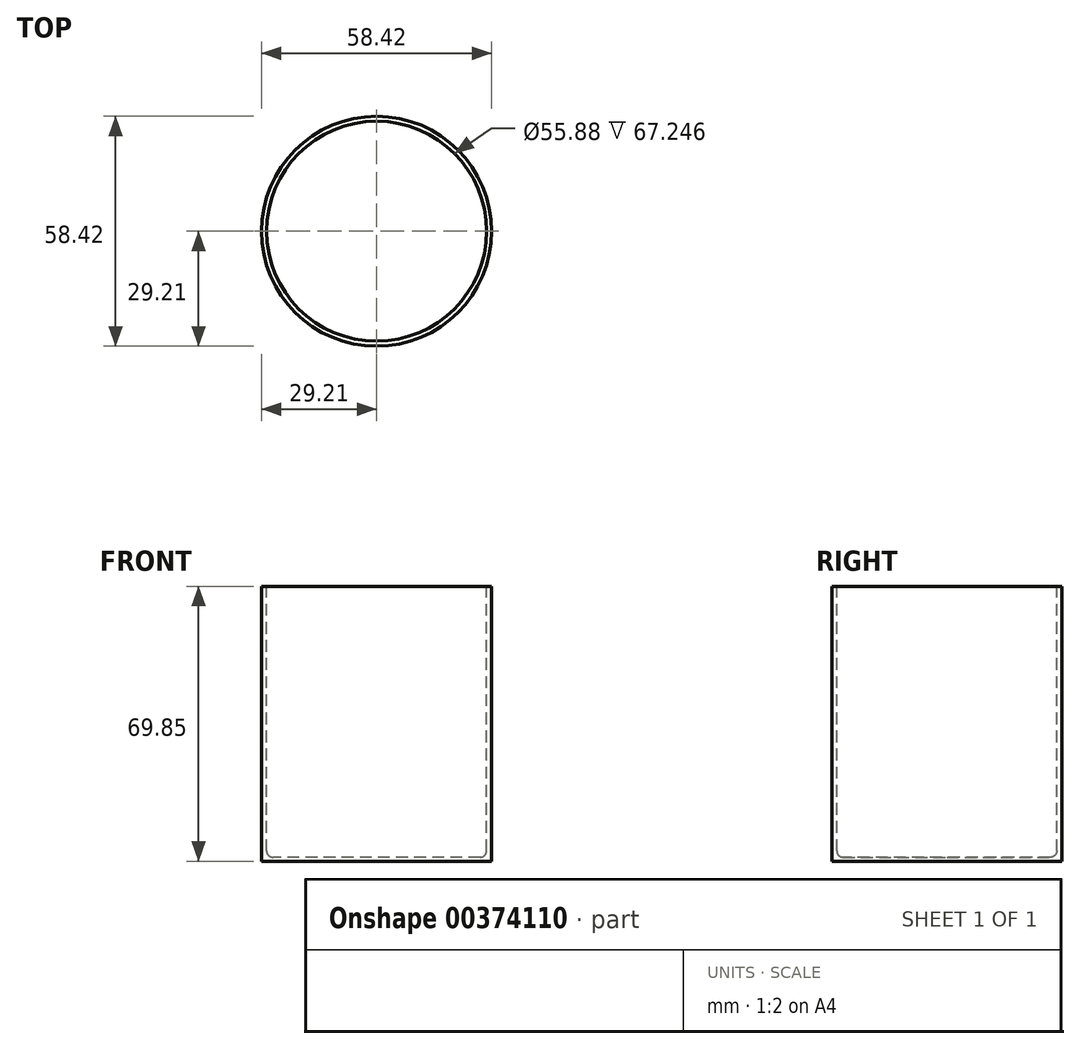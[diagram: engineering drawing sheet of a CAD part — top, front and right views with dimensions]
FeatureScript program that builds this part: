
annotation { "Feature Type Name" : "Feature", "Feature Type Description" : "" }
export const myFeature = defineFeature(function(context is Context, id is Id, definition is map)
    precondition{}
    {
        {
            var Q0;
            Q0=qCreatedBy(makeId("Top.planeOp"),FACE);
            var sketch = newSketch(context, id + "F0", { "sketchPlane" : qUnion([Q0])});
            skCircle(sketch, "E0", {"center": v(0, 0) * mm, "radius": 29.21 * mm});
            skSolve(sketch);
        }
        {
            var Q0;
            Q0=qSketchRegion(id+"F0",true);
            extrude(context, id + "F1", {"entities" : qUnion([Q0]), "depth" : 69.85 * mm});
        }
        {
            var Q0;
            Q0=makeQuery(id+"F1.opExtrude","CAP_FACE",FACE,{"disambiguationData":[OSD([sQuery(id+"F0.wireOp",EDGE,"E0")])],"isStart":false});
            var sketch = newSketch(context, id + "F2", { "sketchPlane" : qUnion([Q0])});
            skCircle(sketch, "E1", {"center": v(0, 0) * mm, "radius": 27.94 * mm});
            skSolve(sketch);
        }
        {
            var Q0;
            Q0=qSketchRegion(id+"F2",true);
            extrude(context, id + "F3", {"entities" : qUnion([Q0]), "operationType" : NewBodyOperationType.REMOVE, "oppositeDirection" : true, "depth" : 68.83 * mm});
        }
        {
            var Q0;
            Q0=makeQuery(id+"F3.boolean.opBoolean","COPY",EDGE,{"derivedFrom":makeQuery(id+"F3.opExtrude","CAP_EDGE",EDGE,{"disambiguationData":[OSD([sQuery(id+"F2.wireOp",EDGE,"E1")])],"isStart":false})});
            fillet(context, id + "F4", {"entities" : qUnion([Q0]), "radius" : 1.59 * mm, "tangentPropagation" : true, "allowEdgeOverflow" : false});
        }
    });
